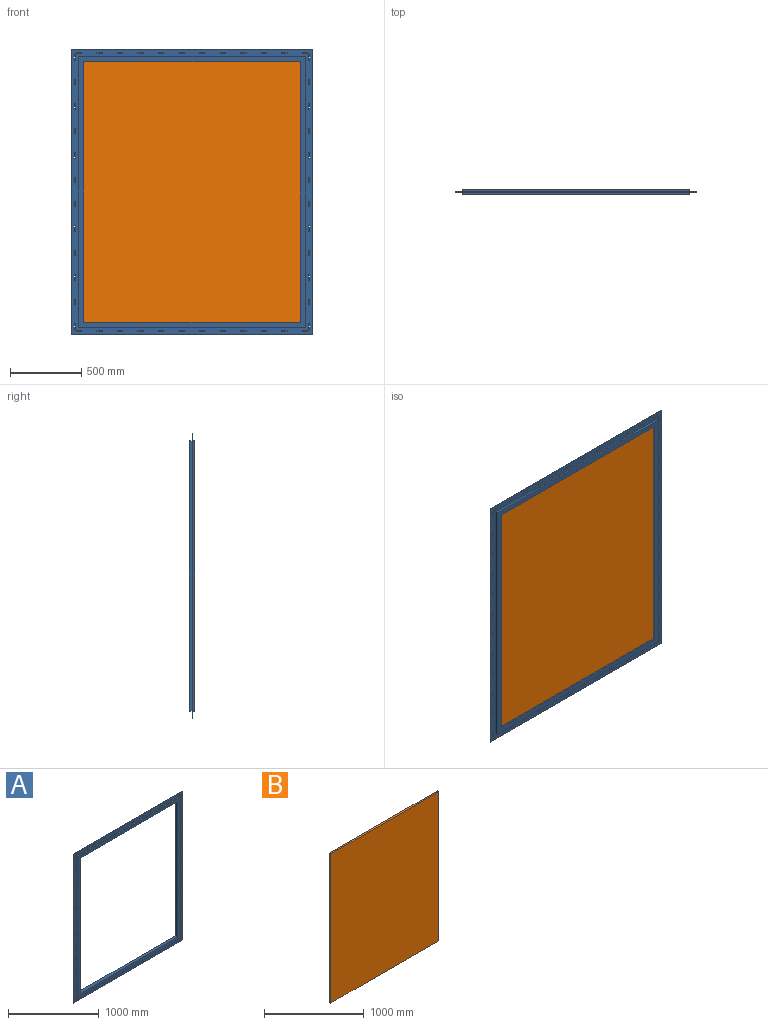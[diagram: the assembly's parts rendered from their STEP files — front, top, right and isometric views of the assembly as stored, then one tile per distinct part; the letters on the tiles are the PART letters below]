
ASSEMBLY  parts=2 mates=1
PART A: 212 faces, bbox 1701.8x38.1x2006.6 mm
  f0: plane 1905x19.05mm, normal (-1,0,0), area 36290.2mm2, adj f1,f3,f13,f211
  f1: plane 1600.2x19.05mm, normal (0,0,-1), area 30483.8mm2, adj f0,f2,f13,f211
  f2: plane 1905x19.05mm, normal (1,0,0), area 36290.3mm2, adj f1,f3,f13,f211
  f3: plane 1600.2x19.05mm, normal (0,0,1), area 30483.8mm2, adj f0,f2,f13,f211
  f4: plane 1828.8x38.1mm, normal (1,0,0), area 69677.3mm2, adj f5,f11,f12,f13
  f5: plane 1524x38.1mm, normal (0,0,-1), area 58064.4mm2, adj f4,f6,f12,f13
  f6: plane 1828.8x38.1mm, normal (-1,0,0), area 69677.3mm2, adj f5,f11,f12,f13
  f7: plane 1905x14.29mm, normal (-1,0,0), area 27217.7mm2, adj f8,f10,f12,f210
  f8: plane 1600.2x14.29mm, normal (0,0,-1), area 22862.9mm2, adj f7,f9,f12,f210
  f9: plane 1905x14.29mm, normal (1,0,0), area 27217.7mm2, adj f8,f10,f12,f210
  f10: plane 1600.2x14.29mm, normal (0,0,1), area 22862.9mm2, adj f7,f9,f12,f210
  f11: plane 1524x38.1mm, normal (0,0,1), area 58064.4mm2, adj f4,f6,f12,f13
  f12: plane 1905x1600.2mm, normal (0,-1,0), area 261289.8mm2, adj f4,f5,f6,f7,f8,f9,f10,f11
  f13: plane 1905x1600.2mm, normal (0,1,0), area 261289.8mm2, adj f0,f1,f2,f3,f4,f5,f6,f11
  f14: plane 1701.8x4.76mm, normal (0,0,-1), area 8104.8mm2, adj f15,f161,f210,f211
  f15: plane 2006.6x4.76mm, normal (1,0,0), area 9556.4mm2, adj f14,f16,f210,f211
  f16: plane 1701.8x4.76mm, normal (0,0,1), area 8104.8mm2, adj f15,f161,f210,f211
  f17: plane 38.1x4.76mm, normal (1,0,0), area 181.5mm2, adj f18,f162,f210,f211
  f18: plane 6.35x4.76mm, normal (0,0,-1), area 30.2mm2, adj f17,f19,f210,f211
  f19: plane 38.1x4.76mm, normal (-1,0,0), area 181.5mm2, adj f18,f162,f210,f211
  f20: plane 6.35x4.76mm, normal (1,0,0), area 30.2mm2, adj f21,f163,f210,f211
  f21: plane 38.1x4.76mm, normal (0,0,-1), area 181.5mm2, adj f20,f22,f210,f211
  f22: plane 6.35x4.76mm, normal (-1,0,0), area 30.2mm2, adj f21,f163,f210,f211
  f23: plane 6.35x4.76mm, normal (1,0,0), area 30.2mm2, adj f24,f164,f210,f211
  f24: plane 38.1x4.76mm, normal (0,0,-1), area 181.5mm2, adj f23,f25,f210,f211
  f25: plane 6.35x4.76mm, normal (-1,0,0), area 30.2mm2, adj f24,f164,f210,f211
  f26: plane 6.35x4.76mm, normal (1,0,0), area 30.2mm2, adj f27,f165,f210,f211
  f27: plane 38.1x4.76mm, normal (0,0,-1), area 181.5mm2, adj f26,f28,f210,f211
  f28: plane 6.35x4.76mm, normal (-1,0,0), area 30.2mm2, adj f27,f165,f210,f211
  f29: plane 6.35x4.76mm, normal (1,0,0), area 30.2mm2, adj f30,f166,f210,f211
  f30: plane 38.1x4.76mm, normal (0,0,-1), area 181.5mm2, adj f29,f31,f210,f211
  f31: plane 6.35x4.76mm, normal (-1,0,0), area 30.2mm2, adj f30,f166,f210,f211
  f32: plane 6.35x4.76mm, normal (1,0,0), area 30.2mm2, adj f33,f167,f210,f211
  f33: plane 38.1x4.76mm, normal (0,0,-1), area 181.5mm2, adj f32,f34,f210,f211
  f34: plane 6.35x4.76mm, normal (-1,0,0), area 30.2mm2, adj f33,f167,f210,f211
  f35: plane 6.35x4.76mm, normal (1,0,0), area 30.2mm2, adj f36,f168,f210,f211
  f36: plane 38.1x4.76mm, normal (0,0,-1), area 181.5mm2, adj f35,f37,f210,f211
  f37: plane 6.35x4.76mm, normal (-1,0,0), area 30.2mm2, adj f36,f168,f210,f211
  f38: plane 6.35x4.76mm, normal (1,0,0), area 30.2mm2, adj f39,f169,f210,f211
  f39: plane 38.1x4.76mm, normal (0,0,-1), area 181.5mm2, adj f38,f40,f210,f211
  f40: plane 6.35x4.76mm, normal (-1,0,0), area 30.2mm2, adj f39,f169,f210,f211
  f41: plane 6.35x4.76mm, normal (1,0,0), area 30.2mm2, adj f42,f170,f210,f211
  f42: plane 38.1x4.76mm, normal (0,0,-1), area 181.5mm2, adj f41,f43,f210,f211
  f43: plane 6.35x4.76mm, normal (-1,0,0), area 30.2mm2, adj f42,f170,f210,f211
  f44: plane 6.35x4.76mm, normal (1,0,0), area 30.2mm2, adj f45,f171,f210,f211
  f45: plane 38.1x4.76mm, normal (0,0,-1), area 181.5mm2, adj f44,f46,f210,f211
  f46: plane 6.35x4.76mm, normal (-1,0,0), area 30.2mm2, adj f45,f171,f210,f211
  f47: plane 6.35x4.76mm, normal (1,0,0), area 30.2mm2, adj f48,f172,f210,f211
  f48: plane 38.1x4.76mm, normal (0,0,-1), area 181.5mm2, adj f47,f49,f210,f211
  f49: plane 6.35x4.76mm, normal (-1,0,0), area 30.2mm2, adj f48,f172,f210,f211
  f50: plane 6.35x4.76mm, normal (1,0,0), area 30.2mm2, adj f51,f173,f210,f211
  f51: plane 38.1x4.76mm, normal (0,0,-1), area 181.5mm2, adj f50,f52,f210,f211
  f52: plane 6.35x4.76mm, normal (-1,0,0), area 30.2mm2, adj f51,f173,f210,f211
  f53: plane 6.35x4.76mm, normal (1,0,0), area 30.2mm2, adj f54,f174,f210,f211
  f54: plane 38.1x4.76mm, normal (0,0,-1), area 181.5mm2, adj f53,f55,f210,f211
  f55: plane 6.35x4.76mm, normal (-1,0,0), area 30.2mm2, adj f54,f174,f210,f211
  f56: plane 6.35x4.76mm, normal (1,0,0), area 30.2mm2, adj f57,f175,f210,f211
  f57: plane 38.1x4.76mm, normal (0,0,-1), area 181.5mm2, adj f56,f58,f210,f211
  f58: plane 6.35x4.76mm, normal (-1,0,0), area 30.2mm2, adj f57,f175,f210,f211
  f59: plane 6.35x4.76mm, normal (1,0,0), area 30.2mm2, adj f60,f176,f210,f211
  f60: plane 38.1x4.76mm, normal (0,0,-1), area 181.5mm2, adj f59,f61,f210,f211
  f61: plane 6.35x4.76mm, normal (-1,0,0), area 30.2mm2, adj f60,f176,f210,f211
  f62: plane 6.35x4.76mm, normal (1,0,0), area 30.2mm2, adj f63,f177,f210,f211
  f63: plane 38.1x4.76mm, normal (0,0,-1), area 181.5mm2, adj f62,f64,f210,f211
  f64: plane 6.35x4.76mm, normal (-1,0,0), area 30.2mm2, adj f63,f177,f210,f211
  f65: plane 6.35x4.76mm, normal (1,0,0), area 30.2mm2, adj f66,f178,f210,f211
  f66: plane 38.1x4.76mm, normal (0,0,-1), area 181.5mm2, adj f65,f67,f210,f211
  f67: plane 6.35x4.76mm, normal (-1,0,0), area 30.2mm2, adj f66,f178,f210,f211
  f68: plane 6.35x4.76mm, normal (1,0,0), area 30.2mm2, adj f69,f179,f210,f211
  f69: plane 38.1x4.76mm, normal (0,0,-1), area 181.5mm2, adj f68,f70,f210,f211
  f70: plane 6.35x4.76mm, normal (-1,0,0), area 30.2mm2, adj f69,f179,f210,f211
  f71: plane 6.35x4.76mm, normal (1,0,0), area 30.2mm2, adj f72,f180,f210,f211
  f72: plane 38.1x4.76mm, normal (0,0,-1), area 181.5mm2, adj f71,f73,f210,f211
  f73: plane 6.35x4.76mm, normal (-1,0,0), area 30.2mm2, adj f72,f180,f210,f211
  f74: plane 6.35x4.76mm, normal (1,0,0), area 30.2mm2, adj f75,f181,f210,f211
  f75: plane 38.1x4.76mm, normal (0,0,-1), area 181.5mm2, adj f74,f76,f210,f211
  f76: plane 6.35x4.76mm, normal (-1,0,0), area 30.2mm2, adj f75,f181,f210,f211
  f77: plane 6.35x4.76mm, normal (1,0,0), area 30.2mm2, adj f78,f182,f210,f211
  f78: plane 38.1x4.76mm, normal (0,0,-1), area 181.5mm2, adj f77,f79,f210,f211
  f79: plane 6.35x4.76mm, normal (-1,0,0), area 30.2mm2, adj f78,f182,f210,f211
  f80: plane 6.35x4.76mm, normal (1,0,0), area 30.2mm2, adj f81,f183,f210,f211
  f81: plane 38.1x4.76mm, normal (0,0,-1), area 181.5mm2, adj f80,f82,f210,f211
  f82: plane 6.35x4.76mm, normal (-1,0,0), area 30.2mm2, adj f81,f183,f210,f211
  f83: plane 6.35x4.76mm, normal (1,0,0), area 30.2mm2, adj f84,f184,f210,f211
  f84: plane 38.1x4.76mm, normal (0,0,-1), area 181.5mm2, adj f83,f85,f210,f211
  f85: plane 6.35x4.76mm, normal (-1,0,0), area 30.2mm2, adj f84,f184,f210,f211
  f86: plane 6.35x4.76mm, normal (1,0,0), area 30.2mm2, adj f87,f185,f210,f211
  f87: plane 38.1x4.76mm, normal (0,0,-1), area 181.5mm2, adj f86,f88,f210,f211
  f88: plane 6.35x4.76mm, normal (-1,0,0), area 30.2mm2, adj f87,f185,f210,f211
  f89: plane 38.1x4.76mm, normal (0,0,1), area 181.5mm2, adj f90,f186,f210,f211
  f90: plane 6.35x4.76mm, normal (1,0,0), area 30.2mm2, adj f89,f91,f210,f211
  f91: plane 38.1x4.76mm, normal (0,0,-1), area 181.5mm2, adj f90,f186,f210,f211
  f92: plane 6.35x4.76mm, normal (0,0,-1), area 30.2mm2, adj f93,f187,f210,f211
  f93: plane 38.1x4.76mm, normal (-1,0,0), area 181.5mm2, adj f92,f94,f210,f211
  f94: plane 6.35x4.76mm, normal (0,0,1), area 30.2mm2, adj f93,f187,f210,f211
  f95: plane 6.35x4.76mm, normal (0,0,-1), area 30.2mm2, adj f96,f188,f210,f211
  f96: plane 38.1x4.76mm, normal (-1,0,0), area 181.5mm2, adj f95,f97,f210,f211
  f97: plane 6.35x4.76mm, normal (0,0,1), area 30.2mm2, adj f96,f188,f210,f211
  f98: plane 6.35x4.76mm, normal (0,0,-1), area 30.2mm2, adj f99,f189,f210,f211
  f99: plane 38.1x4.76mm, normal (-1,0,0), area 181.5mm2, adj f98,f100,f210,f211
  f100: plane 6.35x4.76mm, normal (0,0,1), area 30.2mm2, adj f99,f189,f210,f211
  f101: plane 6.35x4.76mm, normal (0,0,-1), area 30.2mm2, adj f102,f190,f210,f211
  f102: plane 38.1x4.76mm, normal (-1,0,0), area 181.5mm2, adj f101,f103,f210,f211
  f103: plane 6.35x4.76mm, normal (0,0,1), area 30.2mm2, adj f102,f190,f210,f211
  f104: plane 6.35x4.76mm, normal (0,0,-1), area 30.2mm2, adj f105,f191,f210,f211
  f105: plane 38.1x4.76mm, normal (-1,0,0), area 181.5mm2, adj f104,f106,f210,f211
  f106: plane 6.35x4.76mm, normal (0,0,1), area 30.2mm2, adj f105,f191,f210,f211
  f107: plane 6.35x4.76mm, normal (0,0,-1), area 30.2mm2, adj f108,f192,f210,f211
  f108: plane 38.1x4.76mm, normal (-1,0,0), area 181.5mm2, adj f107,f109,f210,f211
  f109: plane 6.35x4.76mm, normal (0,0,1), area 30.2mm2, adj f108,f192,f210,f211
  f110: plane 6.35x4.76mm, normal (0,0,-1), area 30.2mm2, adj f111,f193,f210,f211
  f111: plane 38.1x4.76mm, normal (-1,0,0), area 181.5mm2, adj f110,f112,f210,f211
  f112: plane 6.35x4.76mm, normal (0,0,1), area 30.2mm2, adj f111,f193,f210,f211
  f113: plane 6.35x4.76mm, normal (0,0,-1), area 30.2mm2, adj f114,f194,f210,f211
  f114: plane 38.1x4.76mm, normal (-1,0,0), area 181.5mm2, adj f113,f115,f210,f211
  f115: plane 6.35x4.76mm, normal (0,0,1), area 30.2mm2, adj f114,f194,f210,f211
  f116: plane 6.35x4.76mm, normal (0,0,-1), area 30.2mm2, adj f117,f195,f210,f211
  f117: plane 38.1x4.76mm, normal (-1,0,0), area 181.5mm2, adj f116,f118,f210,f211
  f118: plane 6.35x4.76mm, normal (0,0,1), area 30.2mm2, adj f117,f195,f210,f211
  f119: plane 6.35x4.76mm, normal (0,0,-1), area 30.2mm2, adj f120,f196,f210,f211
  f120: plane 38.1x4.76mm, normal (-1,0,0), area 181.5mm2, adj f119,f121,f210,f211
  f121: plane 6.35x4.76mm, normal (0,0,1), area 30.2mm2, adj f120,f196,f210,f211
  f122: plane 6.35x4.76mm, normal (0,0,-1), area 30.2mm2, adj f123,f197,f210,f211
  f123: plane 38.1x4.76mm, normal (-1,0,0), area 181.5mm2, adj f122,f124,f210,f211
  f124: plane 6.35x4.76mm, normal (0,0,1), area 30.2mm2, adj f123,f197,f210,f211
  f125: plane 6.35x4.76mm, normal (0,0,-1), area 30.2mm2, adj f126,f198,f210,f211
  f126: plane 38.1x4.76mm, normal (-1,0,0), area 181.5mm2, adj f125,f127,f210,f211
  f127: plane 6.35x4.76mm, normal (0,0,1), area 30.2mm2, adj f126,f198,f210,f211
  f128: plane 6.35x4.76mm, normal (0,0,-1), area 30.2mm2, adj f129,f199,f210,f211
  f129: plane 38.1x4.76mm, normal (-1,0,0), area 181.5mm2, adj f128,f130,f210,f211
  f130: plane 6.35x4.76mm, normal (0,0,1), area 30.2mm2, adj f129,f199,f210,f211
  f131: plane 6.35x4.76mm, normal (0,0,-1), area 30.2mm2, adj f132,f200,f210,f211
  f132: plane 38.1x4.76mm, normal (-1,0,0), area 181.5mm2, adj f131,f133,f210,f211
  f133: plane 6.35x4.76mm, normal (0,0,1), area 30.2mm2, adj f132,f200,f210,f211
  f134: plane 6.35x4.76mm, normal (0,0,-1), area 30.2mm2, adj f135,f201,f210,f211
  f135: plane 38.1x4.76mm, normal (-1,0,0), area 181.5mm2, adj f134,f136,f210,f211
  f136: plane 6.35x4.76mm, normal (0,0,1), area 30.2mm2, adj f135,f201,f210,f211
  f137: plane 6.35x4.76mm, normal (0,0,-1), area 30.2mm2, adj f138,f202,f210,f211
  f138: plane 38.1x4.76mm, normal (-1,0,0), area 181.5mm2, adj f137,f139,f210,f211
  f139: plane 6.35x4.76mm, normal (0,0,1), area 30.2mm2, adj f138,f202,f210,f211
  f140: plane 6.35x4.76mm, normal (0,0,-1), area 30.2mm2, adj f141,f203,f210,f211
  f141: plane 38.1x4.76mm, normal (-1,0,0), area 181.5mm2, adj f140,f142,f210,f211
  f142: plane 6.35x4.76mm, normal (0,0,1), area 30.2mm2, adj f141,f203,f210,f211
  f143: plane 6.35x4.76mm, normal (0,0,-1), area 30.2mm2, adj f144,f204,f210,f211
  f144: plane 38.1x4.76mm, normal (-1,0,0), area 181.5mm2, adj f143,f145,f210,f211
  f145: plane 6.35x4.76mm, normal (0,0,1), area 30.2mm2, adj f144,f204,f210,f211
  f146: plane 6.35x4.76mm, normal (0,0,-1), area 30.2mm2, adj f147,f205,f210,f211
  f147: plane 38.1x4.76mm, normal (-1,0,0), area 181.5mm2, adj f146,f148,f210,f211
  f148: plane 6.35x4.76mm, normal (0,0,1), area 30.2mm2, adj f147,f205,f210,f211
  f149: plane 6.35x4.76mm, normal (0,0,-1), area 30.2mm2, adj f150,f206,f210,f211
  f150: plane 38.1x4.76mm, normal (-1,0,0), area 181.5mm2, adj f149,f151,f210,f211
  f151: plane 6.35x4.76mm, normal (0,0,1), area 30.2mm2, adj f150,f206,f210,f211
  f152: plane 6.35x4.76mm, normal (0,0,-1), area 30.2mm2, adj f153,f207,f210,f211
  f153: plane 38.1x4.76mm, normal (-1,0,0), area 181.5mm2, adj f152,f154,f210,f211
  f154: plane 6.35x4.76mm, normal (0,0,1), area 30.2mm2, adj f153,f207,f210,f211
  f155: plane 6.35x4.76mm, normal (0,0,-1), area 30.2mm2, adj f156,f208,f210,f211
  f156: plane 38.1x4.76mm, normal (-1,0,0), area 181.5mm2, adj f155,f157,f210,f211
  f157: plane 6.35x4.76mm, normal (0,0,1), area 30.2mm2, adj f156,f208,f210,f211
  f158: plane 6.35x4.76mm, normal (0,0,-1), area 30.2mm2, adj f159,f209,f210,f211
  f159: plane 38.1x4.76mm, normal (-1,0,0), area 181.5mm2, adj f158,f160,f210,f211
  f160: plane 6.35x4.76mm, normal (0,0,1), area 30.2mm2, adj f159,f209,f210,f211
  f161: plane 2006.6x4.76mm, normal (-1,0,0), area 9556.4mm2, adj f14,f16,f210,f211
  f162: plane 6.35x4.76mm, normal (0,0,1), area 30.2mm2, adj f17,f19,f210,f211
  f163: plane 38.1x4.76mm, normal (0,0,1), area 181.5mm2, adj f20,f22,f210,f211
  f164: plane 38.1x4.76mm, normal (0,0,1), area 181.5mm2, adj f23,f25,f210,f211
  f165: plane 38.1x4.76mm, normal (0,0,1), area 181.5mm2, adj f26,f28,f210,f211
  f166: plane 38.1x4.76mm, normal (0,0,1), area 181.5mm2, adj f29,f31,f210,f211
  f167: plane 38.1x4.76mm, normal (0,0,1), area 181.5mm2, adj f32,f34,f210,f211
  f168: plane 38.1x4.76mm, normal (0,0,1), area 181.5mm2, adj f35,f37,f210,f211
  f169: plane 38.1x4.76mm, normal (0,0,1), area 181.5mm2, adj f38,f40,f210,f211
  f170: plane 38.1x4.76mm, normal (0,0,1), area 181.5mm2, adj f41,f43,f210,f211
  f171: plane 38.1x4.76mm, normal (0,0,1), area 181.5mm2, adj f44,f46,f210,f211
  f172: plane 38.1x4.76mm, normal (0,0,1), area 181.5mm2, adj f47,f49,f210,f211
  f173: plane 38.1x4.76mm, normal (0,0,1), area 181.5mm2, adj f50,f52,f210,f211
  f174: plane 38.1x4.76mm, normal (0,0,1), area 181.5mm2, adj f53,f55,f210,f211
  f175: plane 38.1x4.76mm, normal (0,0,1), area 181.5mm2, adj f56,f58,f210,f211
  f176: plane 38.1x4.76mm, normal (0,0,1), area 181.5mm2, adj f59,f61,f210,f211
  f177: plane 38.1x4.76mm, normal (0,0,1), area 181.5mm2, adj f62,f64,f210,f211
  f178: plane 38.1x4.76mm, normal (0,0,1), area 181.5mm2, adj f65,f67,f210,f211
  f179: plane 38.1x4.76mm, normal (0,0,1), area 181.5mm2, adj f68,f70,f210,f211
  f180: plane 38.1x4.76mm, normal (0,0,1), area 181.5mm2, adj f71,f73,f210,f211
  f181: plane 38.1x4.76mm, normal (0,0,1), area 181.5mm2, adj f74,f76,f210,f211
  f182: plane 38.1x4.76mm, normal (0,0,1), area 181.5mm2, adj f77,f79,f210,f211
  f183: plane 38.1x4.76mm, normal (0,0,1), area 181.5mm2, adj f80,f82,f210,f211
  f184: plane 38.1x4.76mm, normal (0,0,1), area 181.5mm2, adj f83,f85,f210,f211
  f185: plane 38.1x4.76mm, normal (0,0,1), area 181.5mm2, adj f86,f88,f210,f211
  f186: plane 6.35x4.76mm, normal (-1,0,0), area 30.2mm2, adj f89,f91,f210,f211
  f187: plane 38.1x4.76mm, normal (1,0,0), area 181.5mm2, adj f92,f94,f210,f211
  f188: plane 38.1x4.76mm, normal (1,0,0), area 181.5mm2, adj f95,f97,f210,f211
  f189: plane 38.1x4.76mm, normal (1,0,0), area 181.5mm2, adj f98,f100,f210,f211
  f190: plane 38.1x4.76mm, normal (1,0,0), area 181.5mm2, adj f101,f103,f210,f211
  f191: plane 38.1x4.76mm, normal (1,0,0), area 181.5mm2, adj f104,f106,f210,f211
  f192: plane 38.1x4.76mm, normal (1,0,0), area 181.5mm2, adj f107,f109,f210,f211
  f193: plane 38.1x4.76mm, normal (1,0,0), area 181.5mm2, adj f110,f112,f210,f211
  f194: plane 38.1x4.76mm, normal (1,0,0), area 181.5mm2, adj f113,f115,f210,f211
  f195: plane 38.1x4.76mm, normal (1,0,0), area 181.5mm2, adj f116,f118,f210,f211
  f196: plane 38.1x4.76mm, normal (1,0,0), area 181.5mm2, adj f119,f121,f210,f211
  f197: plane 38.1x4.76mm, normal (1,0,0), area 181.5mm2, adj f122,f124,f210,f211
  f198: plane 38.1x4.76mm, normal (1,0,0), area 181.5mm2, adj f125,f127,f210,f211
  f199: plane 38.1x4.76mm, normal (1,0,0), area 181.5mm2, adj f128,f130,f210,f211
  f200: plane 38.1x4.76mm, normal (1,0,0), area 181.5mm2, adj f131,f133,f210,f211
  f201: plane 38.1x4.76mm, normal (1,0,0), area 181.5mm2, adj f134,f136,f210,f211
  f202: plane 38.1x4.76mm, normal (1,0,0), area 181.5mm2, adj f137,f139,f210,f211
  f203: plane 38.1x4.76mm, normal (1,0,0), area 181.5mm2, adj f140,f142,f210,f211
  f204: plane 38.1x4.76mm, normal (1,0,0), area 181.5mm2, adj f143,f145,f210,f211
  f205: plane 38.1x4.76mm, normal (1,0,0), area 181.5mm2, adj f146,f148,f210,f211
  f206: plane 38.1x4.76mm, normal (1,0,0), area 181.5mm2, adj f149,f151,f210,f211
  f207: plane 38.1x4.76mm, normal (1,0,0), area 181.5mm2, adj f152,f154,f210,f211
  f208: plane 38.1x4.76mm, normal (1,0,0), area 181.5mm2, adj f155,f157,f210,f211
  f209: plane 38.1x4.76mm, normal (1,0,0), area 181.5mm2, adj f158,f160,f210,f211
  f210: plane 2006.6x1701.8mm, normal (0,-1,0), area 354838mm2, adj f7,f8,f9,f10,f14,f15,f16,f17
  f211: plane 2006.6x1701.8mm, normal (0,1,0), area 354838mm2, adj f0,f1,f2,f3,f14,f15,f16,f17
PART B: 6 faces, bbox 1524x19.1x1828.8 mm
  f0: plane 1524x19.05mm, normal (0,0,-1), area 29032.2mm2, adj f1,f3,f4,f5
  f1: plane 1828.8x19.05mm, normal (1,0,0), area 34838.6mm2, adj f0,f2,f4,f5
  f2: plane 1524x19.05mm, normal (0,0,1), area 29032.2mm2, adj f1,f3,f4,f5
  f3: plane 1828.8x19.05mm, normal (-1,0,0), area 34838.6mm2, adj f0,f2,f4,f5
  f4: plane 1828.8x1524mm, normal (0,-1,0), area 2787091.2mm2, adj f0,f1,f2,f3
  f5: plane 1828.8x1524mm, normal (0,1,0), area 2787091.2mm2, adj f0,f1,f2,f3
PLACE A t=(132.35,1.22,68.04)mm
PLACE B t=(132.35,10.75,68.04)mm
MATE parallel B.f4 <-> A.f12  axis (0,-1,0) through (-629.65,-8.3,982.44)mm
